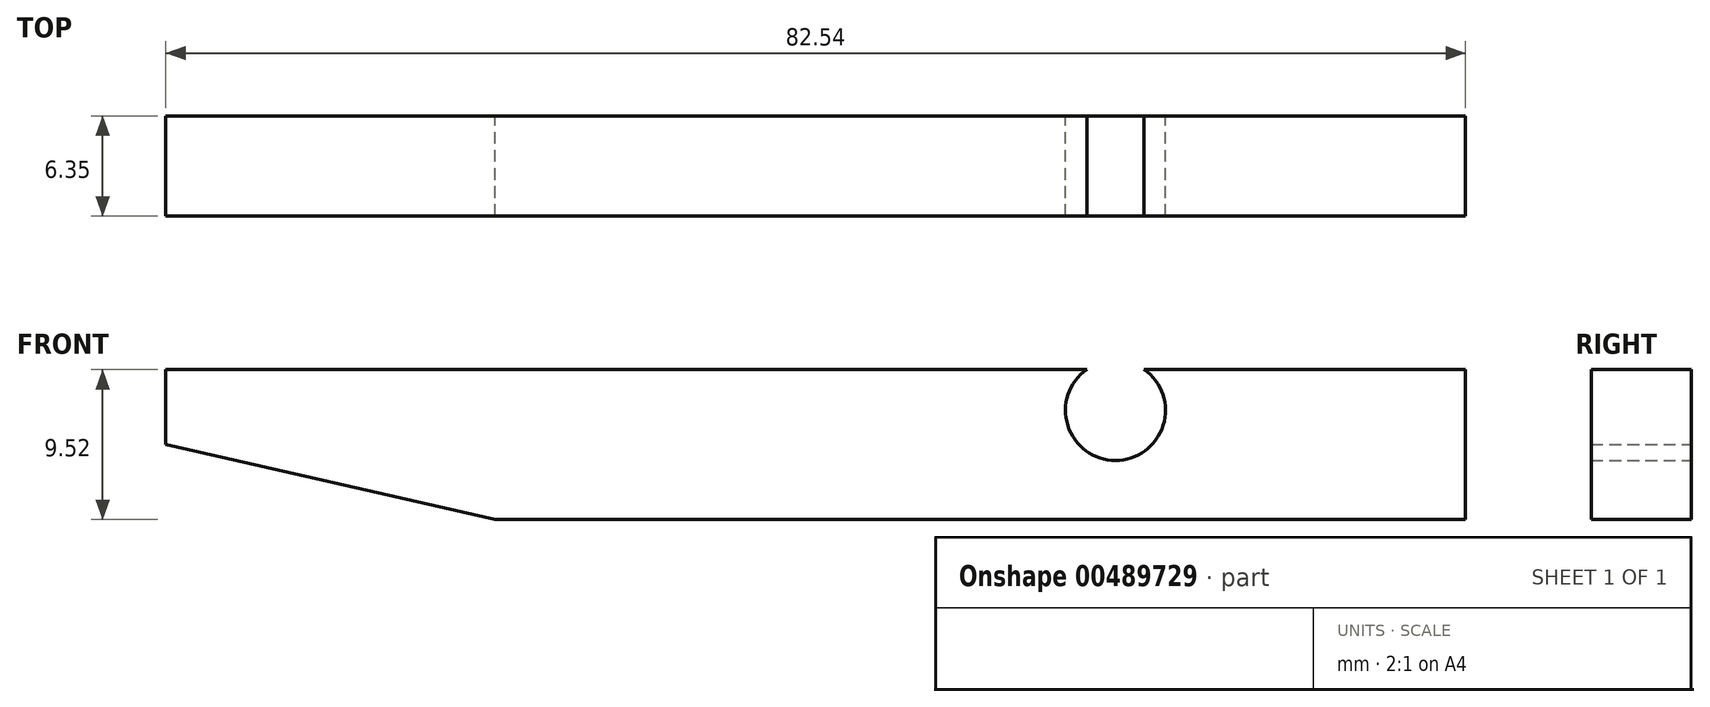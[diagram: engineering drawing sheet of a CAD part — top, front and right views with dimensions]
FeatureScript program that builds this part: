
annotation { "Feature Type Name" : "Feature", "Feature Type Description" : "" }
export const myFeature = defineFeature(function(context is Context, id is Id, definition is map)
    precondition{}
    {
        {
            var Q0;
            Q0=qCreatedBy(makeId("Front.planeOp"),FACE);
            var sketch = newSketch(context, id + "F0", { "sketchPlane" : qUnion([Q0])});
            skLineSegment(sketch, "E0.bottom", {"start": v(-41.27, 4.76) * mm, "end": v(17.23, 4.76) * mm});
            skLineSegment(sketch, "E0.top", {"start": v(-20.36, -4.76) * mm, "end": v(41.27, -4.76) * mm});
            skLineSegment(sketch, "E0.left", {"start": v(-41.27, 4.76) * mm, "end": v(-41.27, 0) * mm});
            skLineSegment(sketch, "E0.right", {"start": v(41.28, 4.76) * mm, "end": v(41.28, -4.76) * mm});
            skLineSegment(sketch, "E1", {"start": v(-41.27, 0) * mm, "end": v(-20.36, -4.76) * mm});
            skArc(sketch, "E2", {"start": v(17.23, 4.76) * mm, "mid": v(19.05, -1.01) * mm, "end": v(20.87, 4.76) * mm});
            skLineSegment(sketch, "E3.trimOffspring", {"start": v(20.87, 4.76) * mm, "end": v(41.27, 4.76) * mm});
            skSolve(sketch);
        }
        {
            var Q0;
            Q0 = qSketchRegion(id + "F0", true);
            extrude(context, id + "F1", {"entities" : qUnion([Q0]), "depth" : 6.35 * mm});
        }
    });
